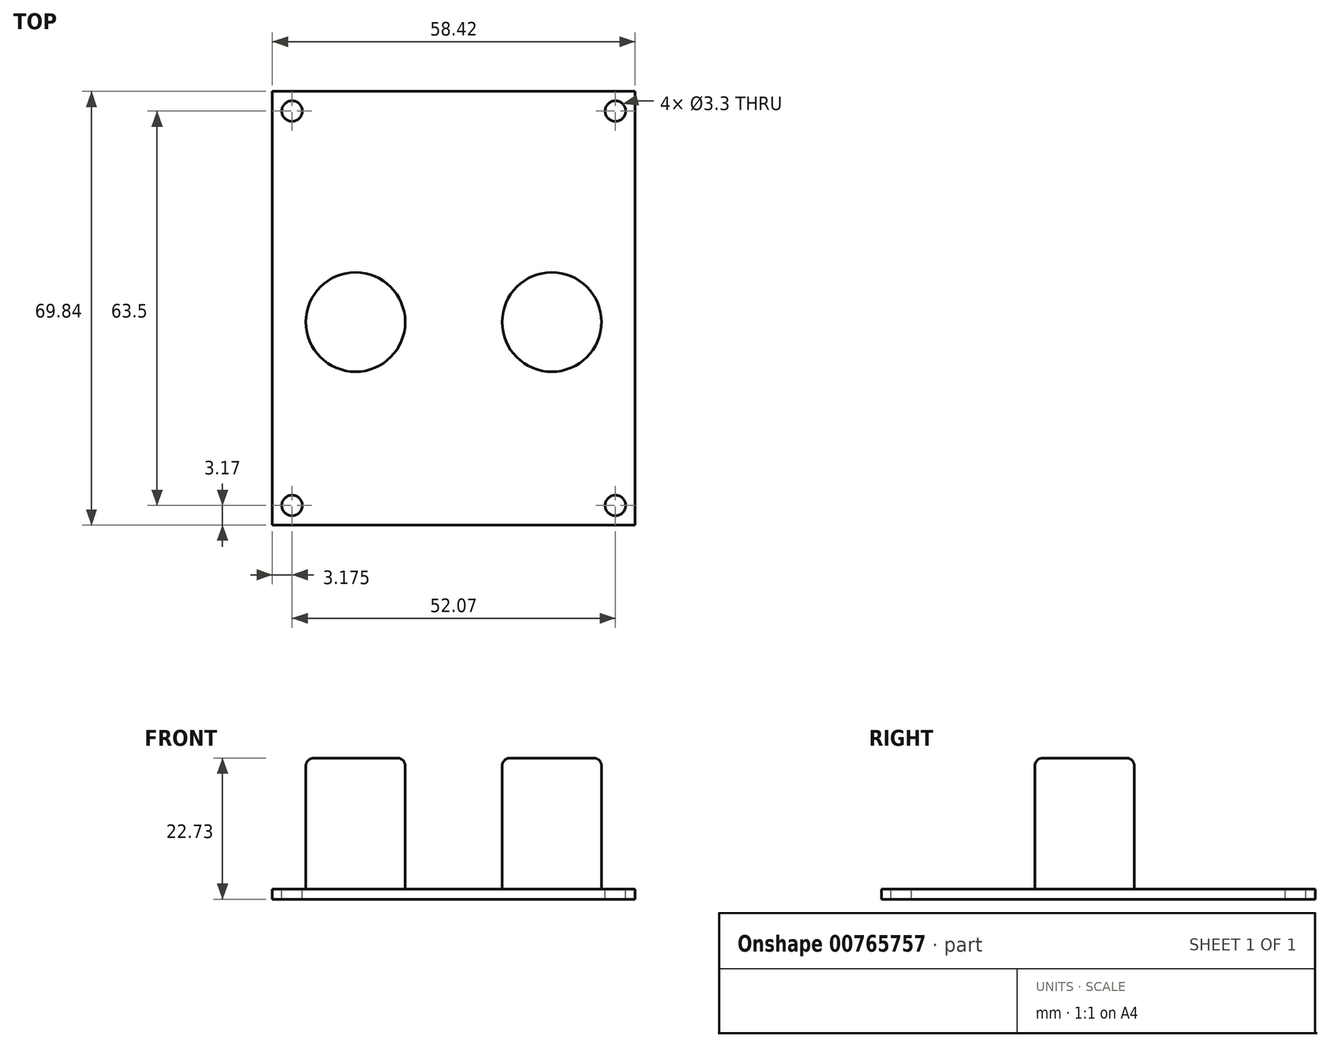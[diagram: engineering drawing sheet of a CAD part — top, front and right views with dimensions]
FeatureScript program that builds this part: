
annotation { "Feature Type Name" : "Feature", "Feature Type Description" : "" }
export const myFeature = defineFeature(function(context is Context, id is Id, definition is map)
    precondition{}
    {
        {
            var Q0;
            Q0=qCreatedBy(makeId("Top.planeOp"),FACE);
            var sketch = newSketch(context, id + "F0", { "sketchPlane" : qUnion([Q0])});
            skLineSegment(sketch, "E0.bottom", {"start": v(29.2, -34.93) * mm, "end": v(-29.21, -34.93) * mm});
            skLineSegment(sketch, "E0.top", {"start": v(29.21, 34.93) * mm, "end": v(-29.21, 34.92) * mm});
            skLineSegment(sketch, "E0.left", {"start": v(29.2, -34.92) * mm, "end": v(29.21, 34.93) * mm});
            skLineSegment(sketch, "E0.right", {"start": v(-29.21, -34.93) * mm, "end": v(-29.21, 34.92) * mm});
            skPoint(sketch, "E0.middle", {"position": v(0, 0) * mm});
            skSolve(sketch);
        }
        {
            var Q0;
            Q0 = qSketchRegion(id + "F0", true);
            extrude(context, id + "F1", {"entities" : qUnion([Q0]), "depth" : 1.62 * mm, "offsetDistance" : 25.4 * mm});
        }
        {
            var Q0;
            Q0=makeQuery(id+"F1.opExtrude","CAP_FACE",FACE,{"disambiguationData":[OSD([sQuery(id+"F0.wireOp",EDGE,"E0.bottom"),sQuery(id+"F0.wireOp",EDGE,"E0.top"),sQuery(id+"F0.wireOp",EDGE,"E0.left"),sQuery(id+"F0.wireOp",EDGE,"E0.right")])],"isStart":false});
            var sketch = newSketch(context, id + "F2", { "sketchPlane" : qUnion([Q0])});
            skCircle(sketch, "E1", {"center": v(-26.04, -31.75) * mm, "radius": 1.65 * mm});
            skCircle(sketch, "E2.MirrorC", {"center": v(26.04, -31.75) * mm, "radius": 1.65 * mm});
            skCircle(sketch, "E3.MirrorC", {"center": v(-26.04, 31.75) * mm, "radius": 1.65 * mm});
            skCircle(sketch, "E4.MirrorC", {"center": v(26.04, 31.75) * mm, "radius": 1.65 * mm});
            skSolve(sketch);
        }
        {
            var Q0;
            Q0 = qSketchRegion(id + "F2", true);
            extrude(context, id + "F3", {"entities" : qUnion([Q0]), "operationType" : NewBodyOperationType.REMOVE, "oppositeDirection" : true, "depth" : 25.4 * mm, "offsetDistance" : 25.4 * mm});
        }
        {
            var Q0;
            Q0=makeQuery(id+"F1.opExtrude","CAP_FACE",FACE,{"disambiguationData":[OSD([sQuery(id+"F0.wireOp",EDGE,"E0.bottom"),sQuery(id+"F0.wireOp",EDGE,"E0.top"),sQuery(id+"F0.wireOp",EDGE,"E0.left"),sQuery(id+"F0.wireOp",EDGE,"E0.right")])],"isStart":false});
            var sketch = newSketch(context, id + "F4", { "sketchPlane" : qUnion([Q0])});
            skCircle(sketch, "E5", {"center": v(-15.81, -2.22) * mm, "radius": 8 * mm});
            skCircle(sketch, "E6", {"center": v(15.8, -2.22) * mm, "radius": 8 * mm});
            skSolve(sketch);
        }
        {
            var Q0;
            Q0 = qSketchRegion(id + "F4", true);
            extrude(context, id + "F5", {"entities" : qUnion([Q0]), "operationType" : NewBodyOperationType.ADD, "depth" : 21.1 * mm, "offsetDistance" : 25.4 * mm});
        }
        {
            var Q0;
            Q0=makeQuery(id+"F5.opExtrude","CAP_EDGE",EDGE,{"disambiguationData":[OSD([sQuery(id+"F4.wireOp",EDGE,"E5")])],"isStart":false});
            var Q1;
            Q1=makeQuery(id+"F5.opExtrude","CAP_EDGE",EDGE,{"disambiguationData":[OSD([sQuery(id+"F4.wireOp",EDGE,"E6")])],"isStart":false});
            fillet(context, id + "F6", {"entities" : qUnion([Q0, Q1]), "radius" : 1.27 * mm, "tangentPropagation" : true, "allowEdgeOverflow" : false});
        }
    });
